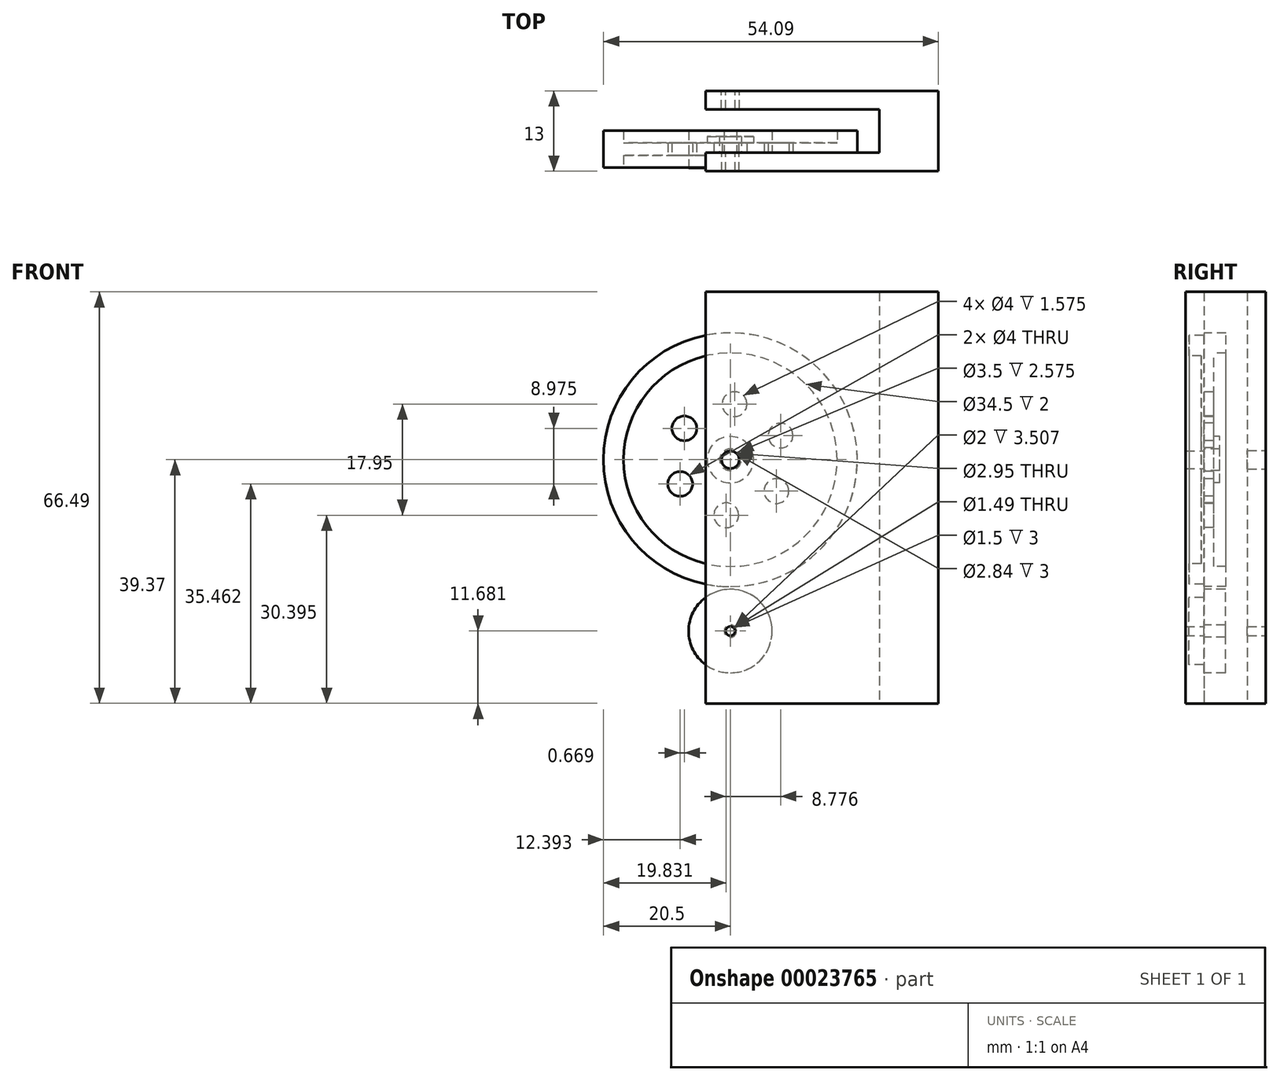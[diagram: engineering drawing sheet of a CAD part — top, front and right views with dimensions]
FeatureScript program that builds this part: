
annotation { "Feature Type Name" : "Feature", "Feature Type Description" : "" }
export const myFeature = defineFeature(function(context is Context, id is Id, definition is map)
    precondition{}
    {
        {
            var Q0;
            Q0=qCreatedBy(makeId("Right.planeOp"),FACE);
            var sketch = newSketch(context, id + "F0", { "sketchPlane" : qUnion([Q0])});
            skLineSegment(sketch, "E0", {"start": v(-14.92, 0) * mm, "end": v(15.03, 0) * mm, "construction": true});
            skLineSegment(sketch, "E1.bottom", {"start": v(-10.42, 1.75) * mm, "end": v(-8.42, 1.75) * mm});
            skLineSegment(sketch, "E1.top", {"start": v(-10.42, 17.25) * mm, "end": v(-8.42, 17.25) * mm});
            skLineSegment(sketch, "E1.left", {"start": v(-10.42, 1.75) * mm, "end": v(-10.42, 17.25) * mm});
            skLineSegment(sketch, "E1.right", {"start": v(-8.42, 1.75) * mm, "end": v(-8.42, 17.25) * mm});
            skLineSegment(sketch, "E2.bottom", {"start": v(-12.42, 17.25) * mm, "end": v(-6.42, 17.25) * mm});
            skLineSegment(sketch, "E2.top", {"start": v(-12.42, 20.5) * mm, "end": v(-6.42, 20.5) * mm});
            skLineSegment(sketch, "E2.left", {"start": v(-12.42, 17.25) * mm, "end": v(-12.42, 20.5) * mm});
            skLineSegment(sketch, "E2.right", {"start": v(-6.42, 17.25) * mm, "end": v(-6.42, 20.5) * mm});
            skLineSegment(sketch, "E3.bottom", {"start": v(-11.42, 1.75) * mm, "end": v(-7.42, 1.75) * mm});
            skLineSegment(sketch, "E3.top", {"start": v(-11.42, 3.75) * mm, "end": v(-7.42, 3.75) * mm});
            skLineSegment(sketch, "E3.left", {"start": v(-11.42, 1.75) * mm, "end": v(-11.42, 3.75) * mm});
            skLineSegment(sketch, "E3.right", {"start": v(-7.42, 1.75) * mm, "end": v(-7.42, 3.75) * mm});
            skSolve(sketch);
        }
        {
            var Q0;
            Q0 = qSketchRegion(id + "F0", true);
            var Q1;
            Q1=sQuery(id+"F0.wireOp",EDGE,"E0");
            revolve(context, id + "F1", {"entities" : qUnion([Q0]), "axis" : qUnion([Q1]), "revolveType" : RevolveType.FULL});
        }
        {
            var Q0;
            Q0=makeQuery(id+"F1.opRevolve","SWEPT_FACE",FACE,{"disambiguationData":[OSD([sQuery(id+"F0.wireOp",EDGE,"E1.left")])]});
            var sketch = newSketch(context, id + "F2", { "sketchPlane" : qUnion([Q0])});
            skCircle(sketch, "E4", {"center": v(0, 0) * mm, "radius": 9 * mm, "construction": true});
            skCircle(sketch, "E5", {"center": v(0.67, 8.98) * mm, "radius": 2 * mm});
            skCircle(sketch, "E6.1.0", {"center": v(8.1, 3.9) * mm, "radius": 2 * mm});
            skCircle(sketch, "E6.2.0", {"center": v(7.44, -5.07) * mm, "radius": 2 * mm});
            skCircle(sketch, "E6.3.0", {"center": v(-0.67, -8.98) * mm, "radius": 2 * mm});
            skCircle(sketch, "E6.4.0", {"center": v(-8.1, -3.9) * mm, "radius": 2 * mm});
            skCircle(sketch, "E6.5.0", {"center": v(-7.44, 5.07) * mm, "radius": 2 * mm});
            skLineSegment(sketch, "E6.anchor1", {"start": v(0, 0) * mm, "end": v(0.67, 8.98) * mm, "construction": true});
            skLineSegment(sketch, "E6.anchor2", {"start": v(0, 0) * mm, "end": v(-7.44, 5.07) * mm, "construction": true});
            skSolve(sketch);
        }
        {
            var Q0;
            Q0=makeQuery(id+"F2.imprint","IMPRINT",FACE,{"disambiguationData":[TD([[makeQuery(id+"F2.imprint","IMPRINT",EDGE,{"derivedFrom":sQuery(id+"F2.wireOp",EDGE,"E5")}),1.0]])]});
            var Q1;
            Q1=makeQuery(id+"F2.imprint","IMPRINT",FACE,{"disambiguationData":[TD([[makeQuery(id+"F2.imprint","IMPRINT",EDGE,{"derivedFrom":sQuery(id+"F2.wireOp",EDGE,"E6.1.0")}),1.0]])]});
            var Q2;
            Q2=makeQuery(id+"F2.imprint","IMPRINT",FACE,{"disambiguationData":[TD([[makeQuery(id+"F2.imprint","IMPRINT",EDGE,{"derivedFrom":sQuery(id+"F2.wireOp",EDGE,"E6.2.0")}),1.0]])]});
            var Q3;
            Q3=makeQuery(id+"F2.imprint","IMPRINT",FACE,{"disambiguationData":[TD([[makeQuery(id+"F2.imprint","IMPRINT",EDGE,{"derivedFrom":sQuery(id+"F2.wireOp",EDGE,"E6.3.0")}),1.0]])]});
            var Q4;
            Q4=makeQuery(id+"F2.imprint","IMPRINT",FACE,{"disambiguationData":[TD([[makeQuery(id+"F2.imprint","IMPRINT",EDGE,{"derivedFrom":sQuery(id+"F2.wireOp",EDGE,"E6.4.0")}),1.0]])]});
            var Q5;
            Q5=makeQuery(id+"F2.imprint","IMPRINT",FACE,{"disambiguationData":[TD([[makeQuery(id+"F2.imprint","IMPRINT",EDGE,{"derivedFrom":sQuery(id+"F2.wireOp",EDGE,"E6.5.0")}),1.0]])]});
            extrude(context, id + "F3", {"entities" : qUnion([Q0, Q1, Q2, Q3, Q4, Q5]), "operationType" : NewBodyOperationType.REMOVE, "endBound" : BoundingType.THROUGH_ALL, "oppositeDirection" : true, "depth" : 25 * mm});
        }
        {
            var Q0;
            Q0=qCreatedBy(makeId("Right.planeOp"),FACE);
            var sketch = newSketch(context, id + "F4", { "sketchPlane" : qUnion([Q0])});
            skLineSegment(sketch, "E7", {"start": v(-10.22, -27.69) * mm, "end": v(14.34, -27.69) * mm, "construction": true});
            skLineSegment(sketch, "E8.bottom", {"start": v(-12.5, -26.69) * mm, "end": v(-6.5, -26.69) * mm});
            skLineSegment(sketch, "E8.top", {"start": v(-12.5, -20.94) * mm, "end": v(-6.5, -20.94) * mm});
            skLineSegment(sketch, "E8.left", {"start": v(-12.5, -26.69) * mm, "end": v(-12.5, -20.94) * mm});
            skLineSegment(sketch, "E8.right", {"start": v(-6.5, -26.69) * mm, "end": v(-6.5, -20.94) * mm});
            skSolve(sketch);
        }
        {
            var Q0;
            Q0 = qSketchRegion(id + "F4", true);
            var Q1;
            Q1=sQuery(id+"F4.wireOp",EDGE,"E7");
            revolve(context, id + "F5", {"entities" : qUnion([Q0]), "axis" : qUnion([Q1]), "revolveType" : RevolveType.FULL});
        }
        {
            var Q0;
            Q0=qCreatedBy(makeId("Front.planeOp"),FACE);
            var sketch = newSketch(context, id + "F6", { "sketchPlane" : qUnion([Q0])});
            skLineSegment(sketch, "E9.bottom", {"start": v(33.6, 27.12) * mm, "end": v(-4.03, 27.12) * mm});
            skLineSegment(sketch, "E9.top", {"start": v(33.6, -39.37) * mm, "end": v(-4.03, -39.37) * mm});
            skLineSegment(sketch, "E9.left", {"start": v(33.6, 27.12) * mm, "end": v(33.6, -39.37) * mm});
            skCircle(sketch, "E10", {"center": v(0, 0) * mm, "radius": 1.47 * mm});
            skCircle(sketch, "E11", {"center": v(0, -27.69) * mm, "radius": 0.75 * mm});
            skLineSegment(sketch, "E12.right", {"start": v(-4.03, 27.12) * mm, "end": v(-4.03, -39.37) * mm});
            skSolve(sketch);
        }
        {
            var Q0;
            Q0 = qSketchRegion(id + "F6", true);
            extrude(context, id + "F7", {"entities" : qUnion([Q0]), "depth" : 3 * mm});
        }
        {
            var Q0;
            Q0=makeQuery(id+"F7.opExtrude","CAP_FACE",FACE,{"disambiguationData":[OSD([sQuery(id+"F6.wireOp",EDGE,"E9.bottom"),sQuery(id+"F6.wireOp",EDGE,"E9.top"),sQuery(id+"F6.wireOp",EDGE,"E9.left"),sQuery(id+"F6.wireOp",EDGE,"E9.right")])],"isStart":false});
            var sketch = newSketch(context, id + "F8", { "sketchPlane" : qUnion([Q0])});
            skLineSegment(sketch, "E13.bottom", {"start": v(33.6, 27.12) * mm, "end": v(24.05, 27.12) * mm});
            skLineSegment(sketch, "E13.top", {"start": v(33.6, -39.37) * mm, "end": v(24.05, -39.37) * mm});
            skLineSegment(sketch, "E13.left", {"start": v(33.6, 27.12) * mm, "end": v(33.6, -39.37) * mm});
            skLineSegment(sketch, "E13.right", {"start": v(24.05, 27.12) * mm, "end": v(24.05, -39.37) * mm});
            skSolve(sketch);
        }
        {
            var Q0;
            Q0 = qSketchRegion(id + "F8", true);
            extrude(context, id + "F9", {"entities" : qUnion([Q0]), "operationType" : NewBodyOperationType.ADD, "depth" : 7 * mm});
        }
        {
            var Q0;
            Q0=makeQuery(id+"F9.opExtrude","CAP_FACE",FACE,{"disambiguationData":[OSD([sQuery(id+"F8.wireOp",EDGE,"E13.bottom"),sQuery(id+"F8.wireOp",EDGE,"E13.top"),sQuery(id+"F8.wireOp",EDGE,"E13.left"),sQuery(id+"F8.wireOp",EDGE,"E13.right")])],"isStart":false});
            var sketch = newSketch(context, id + "F10", { "sketchPlane" : qUnion([Q0])});
            skLineSegment(sketch, "E14.bottom", {"start": v(33.6, 27.12) * mm, "end": v(-4.03, 27.12) * mm});
            skLineSegment(sketch, "E14.top", {"start": v(33.6, -39.37) * mm, "end": v(-4.03, -39.37) * mm});
            skLineSegment(sketch, "E14.left", {"start": v(33.6, 27.12) * mm, "end": v(33.6, -39.37) * mm});
            skLineSegment(sketch, "E14.right", {"start": v(-4.03, 27.12) * mm, "end": v(-4.03, -39.37) * mm});
            skCircle(sketch, "E15", {"center": v(0, 0) * mm, "radius": 1.42 * mm});
            skCircle(sketch, "E16", {"center": v(0, -27.69) * mm, "radius": 0.75 * mm});
            skSolve(sketch);
        }
        {
            var Q0;
            Q0 = qSketchRegion(id + "F10", true);
            extrude(context, id + "F11", {"entities" : qUnion([Q0]), "operationType" : NewBodyOperationType.ADD, "depth" : 3 * mm});
        }
    });
